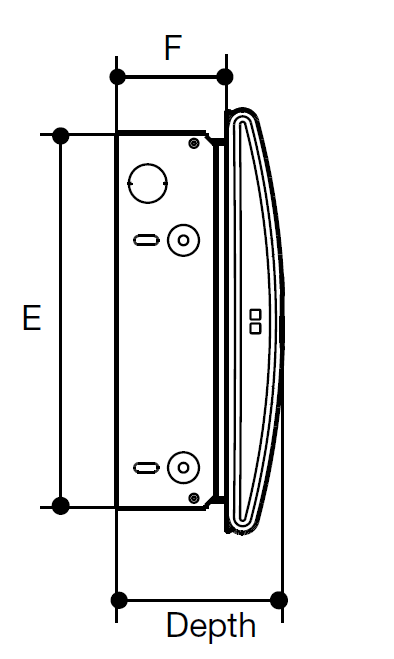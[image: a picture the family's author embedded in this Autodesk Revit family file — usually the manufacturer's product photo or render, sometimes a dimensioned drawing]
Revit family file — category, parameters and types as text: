
# Revit family: Hager-SM_Design_50-Configurable_High_Integrity-NoHosted-UK-en
name_source: partatom
category: Electrical Equipment
units: mm (PartAtom-declared; Revit-internal decimal feet)

## family parameters
Always vertical = Yes
Cut with Voids When Loaded = No
Panel Configuration = Two Columns, Circuits Across
Part Type = Panelboard
Room Calculation Point = No
Round Connector Dimension = Use Diameter
Shared = No
Work Plane-Based = Yes

## types (4) — shared parameters
Classification.Uniclass.Pr.Description = Control circuit device enclosures
Classification.Uniclass.Pr.Number = Pr_80_77_28_16
Default Elevation = 1219 mm
EF000007 - Colour = EV000202 - White
EF000040 - Height = 284 mm  [stored 0.931759 ft]
EF000049 - Depth = 105 mm  [stored 0.344488 ft]
EF000116 - RAL-number = 9010
EF000118 - With mounting plate = No
EF000218 - Built-in depth = 72 mm  [stored 0.23622 ft]
EF000266 - Number of rows = 1
EF000332 - Built-in height = 252 mm  [stored 0.826772 ft]
EF000339 - Type of cover = EV001012 - Cover
EF001062 - EMC-version = No
EF001088 - Extension possible = Yes
EF001134 - DIN-rail = No
EF001596 - Material housing = EV000179 - Steel
EF004462 - Type of closure = EV000154 - Other
EF005474 - Degree of protection (IP) = EV009848 - IP2XC
EF006244 - Transparent cover/door = No
EF006306 - With lock = No
EF009212 - Cover model = EV000116 - Closed
EF015941 - Signal passing door = No
HG000002 - With door or cover = Yes
HG000003 - Range = Surface Mounting Consumer Units
HG000005 - Thickness = 3 mm  [stored 0.00984252 ft]
HG000017 - Distance between poles = 18 mm  [stored 0.0590551 ft]
Manufacturer = Hager
Type Comments = Surface Mounting Consumer Units
zero-valued in all types: Cost, EF001131 - Internal depth, EF002950 - Width in number of modular spacings

## per-type parameters (varying)
| type | EF000003 - Mounting method | EF000008 - Width | EF000846 - Built-in width | EF015776 - Earthing terminal block | EF015777 - Neutral terminal block | HG000004 - Manufacturer reference | HG000006 - Flush mounted | Model |
| Recessed mounted P2XC W467 H284 D105  Modular spacings - VSR910CUSPD | EV000383 - Flush mounted (plaster) | 467 mm  [stored 1.53215 ft] | 406 mm  [stored 1.33202 ft] | Yes | Yes | VSR910CUSPD | Yes | VSR910CUSPD |
| Surface mounted P2XC W431 H284 D105  Modular spacings - VSR910CU | EV000384 - Surface mounted (plaster) | 431 mm  [stored 1.41404 ft] | 370 mm  [stored 1.21391 ft] | No | No | VSR910CU | No | VSR910CU |
| Surface mounted P2XC W467 H284 D105  Modular spacings - VSR912CU | EV000384 - Surface mounted (plaster) | 467 mm  [stored 1.53215 ft] | 406 mm  [stored 1.33202 ft] | No | Yes | VSR912CU | No | VSR912CU |
| Surface mounted P2XC W539 H284 D105  Modular spacings - VSR916CU | EV000384 - Surface mounted (plaster) | 539 mm  [stored 1.76837 ft] | 478 mm  [stored 1.56824 ft] | Yes | Yes | VSR916CU | No | VSR916CU |

note: [stored X ft] marks values corroborated as IEEE doubles in the binary element streams (Revit-internal decimal feet)

## geometry (parser evidence)
native form markers: Blend x4, Revolve x3, Sweep x13
no freeform markers — native parametric forms only
